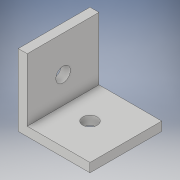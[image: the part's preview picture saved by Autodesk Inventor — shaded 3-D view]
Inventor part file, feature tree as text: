
AUTODESK INVENTOR PART (.ipt)
format: ipt  version: 2018 (Build 220112000, 112)  size: 113,664 bytes
history: native  units: in
note: dims shown in document units (in); Inventor stores cm internally (conversion verified against a paired STEP export)
features: extrude x3, sketch x3
ambient origin geometry x8: Origin, YZ Plane, XZ Plane, XY Plane, X Axis, Y Axis, Z Axis, Center Point
bodies: Solid1 (feature_tree)
feature tree (6):
  extrude  "Extrusion1"  Depth=1.0in
  extrude  "Extrusion2"  Depth=0.125in
  extrude  "Extrusion3"  Depth=1.0in
  sketch  "Sketch1"  dims[d0=0.125in d1=1.0in]
  sketch  "Sketch2"  dims[d2=1.0in d3=0.125in]
  sketch  "Sketch3"  dims[d4=1.0in d5=0.0in d6=0.5in d7=0.2031in d8=1.0in d9=0.0in d10=0.5in d11=0.2031in d12=1.0in d13=0.0in]
